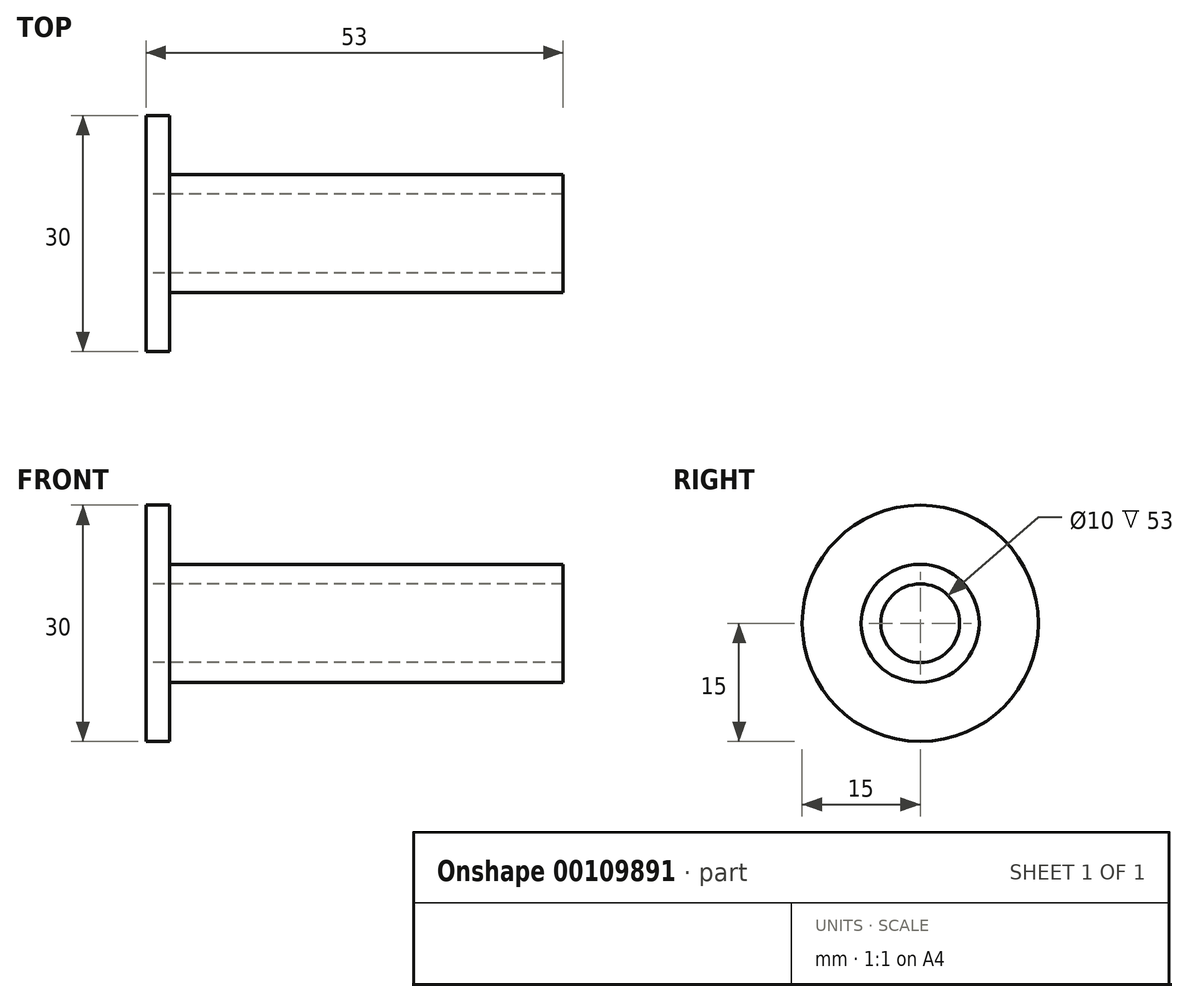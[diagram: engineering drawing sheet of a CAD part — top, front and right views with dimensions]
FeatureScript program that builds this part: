
annotation { "Feature Type Name" : "Feature", "Feature Type Description" : "" }
export const myFeature = defineFeature(function(context is Context, id is Id, definition is map)
    precondition{}
    {
        {
            var Q0;
            Q0=qCreatedBy(makeId("Front.planeOp"),FACE);
            var sketch = newSketch(context, id + "F0", { "sketchPlane" : qUnion([Q0])});
            skLineSegment(sketch, "E0", {"start": v(1, 5) * mm, "end": v(1, 15) * mm});
            skLineSegment(sketch, "E1", {"start": v(1, 15) * mm, "end": v(4, 15) * mm});
            skLineSegment(sketch, "E2", {"start": v(4, 15) * mm, "end": v(4, 7.5) * mm});
            skLineSegment(sketch, "E3", {"start": v(4, 7.5) * mm, "end": v(54, 7.5) * mm});
            skLineSegment(sketch, "E4", {"start": v(54, 7.5) * mm, "end": v(54, 5) * mm});
            skLineSegment(sketch, "E5", {"start": v(54, 5) * mm, "end": v(1, 5) * mm});
            skLineSegment(sketch, "E6", {"start": v(0, 0) * mm, "end": v(60, 0) * mm, "construction": true});
            skSolve(sketch);
        }
        {
            var Q0;
            Q0=makeQuery(id+"F0.imprint","IMPRINT",FACE,{"disambiguationData":[TD([[makeQuery(id+"F0.imprint","IMPRINT",EDGE,{"derivedFrom":sQuery(id+"F0.wireOp",EDGE,"E0")}),-1.0]])]});
            var Q1;
            Q1=sQuery(id+"F0.wireOp",EDGE,"E6");
            revolve(context, id + "F1", {"entities" : qUnion([Q0]), "axis" : qUnion([Q1]), "revolveType" : RevolveType.FULL});
        }
    });
